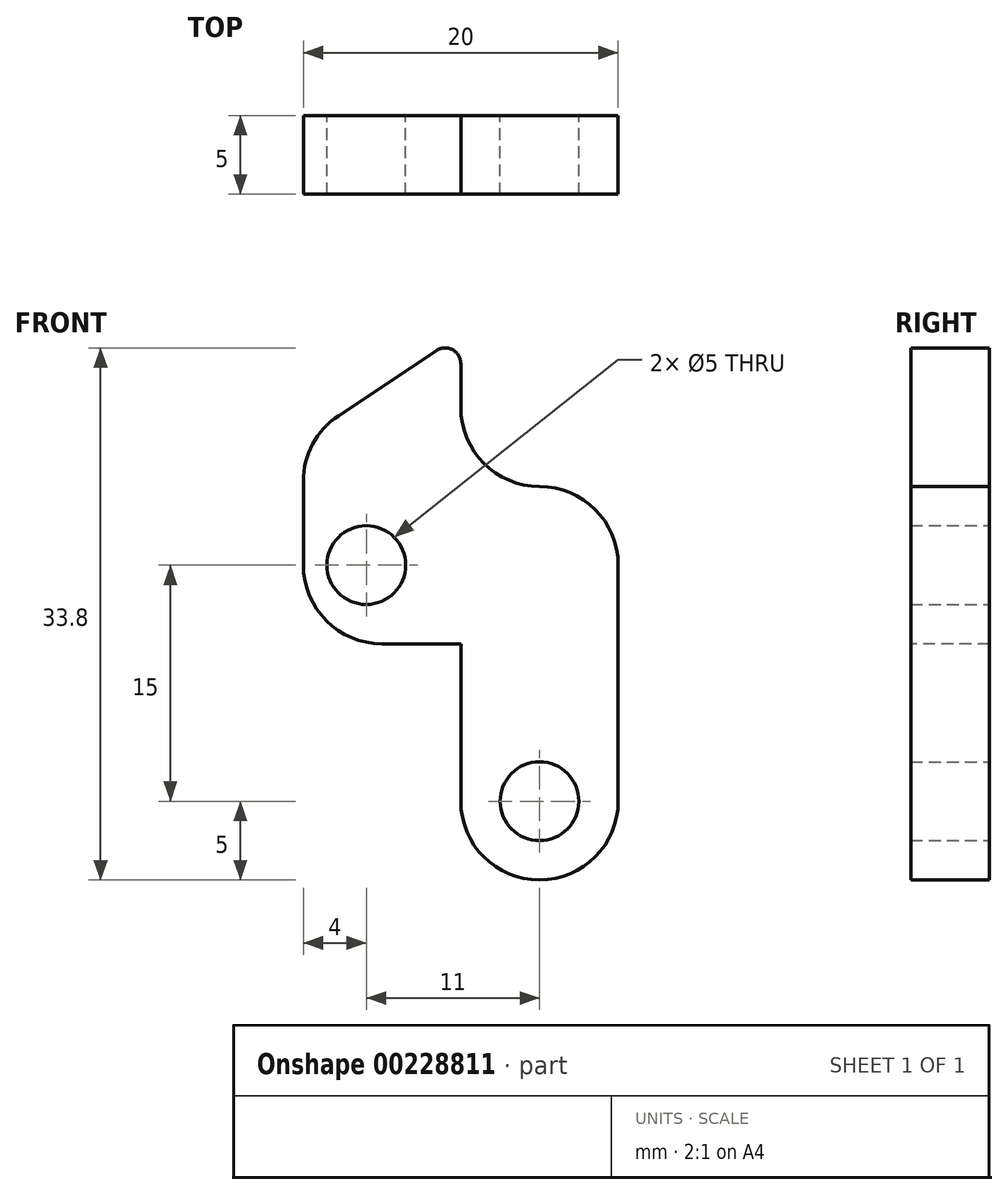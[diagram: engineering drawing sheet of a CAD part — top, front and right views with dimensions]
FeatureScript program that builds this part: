
annotation { "Feature Type Name" : "Feature", "Feature Type Description" : "" }
export const myFeature = defineFeature(function(context is Context, id is Id, definition is map)
    precondition{}
    {
        {
            var Q0;
            Q0=qCreatedBy(makeId("Front.planeOp"),FACE);
            var sketch = newSketch(context, id + "F0", { "sketchPlane" : qUnion([Q0])});
            skLineSegment(sketch, "E0.bottom", {"start": v(-10, 23) * mm, "end": v(0, 23) * mm});
            skLineSegment(sketch, "E0.top", {"start": v(-10, 0) * mm, "end": v(0, 0) * mm});
            skLineSegment(sketch, "E0.left", {"start": v(-10, 23) * mm, "end": v(-10, 0) * mm});
            skLineSegment(sketch, "E0.right", {"start": v(0, 23) * mm, "end": v(0, 0) * mm});
            skLineSegment(sketch, "E1.bottom", {"start": v(10, 0) * mm, "end": v(0, 0) * mm});
            skLineSegment(sketch, "E1.top", {"start": v(10, 10) * mm, "end": v(0, 10) * mm});
            skLineSegment(sketch, "E1.left", {"start": v(10, 0) * mm, "end": v(10, 10) * mm});
            skLineSegment(sketch, "E1.right", {"start": v(0, 0) * mm, "end": v(0, 10) * mm});
            skCircle(sketch, "E2", {"center": v(-6, 5) * mm, "radius": 2.5 * mm});
            skSolve(sketch);
        }
        {
            var Q0;
            Q0=makeQuery(id+"F0.imprint","IMPRINT",FACE,{"disambiguationData":[TD([[makeQuery(id+"F0.imprint","IMPRINT",EDGE,{"derivedFrom":sQuery(id+"F0.wireOp",EDGE,"E0.bottom")}),-1.0]])]});
            var Q1;
            Q1=makeQuery(id+"F0.imprint","IMPRINT",FACE,{"disambiguationData":[TD([[makeQuery(id+"F0.imprint","IMPRINT",EDGE,{"derivedFrom":sQuery(id+"F0.wireOp",EDGE,"E1.bottom")}),-1.0]])]});
            extrude(context, id + "F1", {"entities" : qUnion([Q0, Q1]), "endBound" : BoundingType.SYMMETRIC, "depth" : 5 * mm});
        }
        {
            var Q0;
            Q0=makeQuery(id+"F1.opExtrude","SWEPT_EDGE",EDGE,{"disambiguationData":[OSD([sQuery(id+"F0.wireOp",EDGE,"E0.bottom"),sQuery(id+"F0.wireOp",EDGE,"E0.left")])]});
            chamfer(context, id + "F2", {"entities" : qUnion([Q0]), "chamferType" : ChamferType.TWO_OFFSETS, "width1" : 10 * mm, "oppositeDirection" : false, "width2" : 15 * mm, "tangentPropagation" : true});
        }
        {
            var Q0;
            Q0=makeQuery(id+"F1.opExtrude","SWEPT_EDGE",EDGE,{"disambiguationData":[OSD([sQuery(id+"F0.wireOp",EDGE,"E0.right"),sQuery(id+"F0.wireOp",EDGE,"E1.top"),sQuery(id+"F0.wireOp",EDGE,"E1.right")])]});
            var Q1;
            Q1=makeQuery(id+"F1.opExtrude","SWEPT_EDGE",EDGE,{"disambiguationData":[OSD([sQuery(id+"F0.wireOp",EDGE,"E1.top"),sQuery(id+"F0.wireOp",EDGE,"E1.left")])]});
            var Q2;
            Q2=makeQuery(id+"F1.opExtrude","SWEPT_EDGE",EDGE,{"disambiguationData":[OSD([sQuery(id+"F0.wireOp",EDGE,"E1.bottom"),sQuery(id+"F0.wireOp",EDGE,"E1.left")])]});
            var Q3;
            Q3=makeQuery(id+"F1.opExtrude","SWEPT_EDGE",EDGE,{"disambiguationData":[OSD([sQuery(id+"F0.wireOp",EDGE,"E0.top"),sQuery(id+"F0.wireOp",EDGE,"E0.left")])]});
            fillet(context, id + "F3", {"entities" : qUnion([Q0, Q1, Q2, Q3]), "radius" : 5 * mm, "tangentPropagation" : true, "allowEdgeOverflow" : false});
        }
        {
            var Q0;
            Q0=makeQuery(id+"F2.opChamfer","BLEND_EDGE",EDGE,{"blendedFrom":[makeQuery(id+"F1.opExtrude","SWEPT_EDGE",EDGE,{"disambiguationData":[OSD([sQuery(id+"F0.wireOp",EDGE,"E0.bottom"),sQuery(id+"F0.wireOp",EDGE,"E0.left")])]}),makeQuery(id+"F1.opExtrude","SWEPT_FACE",FACE,{"disambiguationData":[OSD([sQuery(id+"F0.wireOp",EDGE,"E0.right")])]})],"blendedInto":[makeQuery(id+"F1.opExtrude","SWEPT_FACE",FACE,{"disambiguationData":[OSD([sQuery(id+"F0.wireOp",EDGE,"E0.right")])]})]});
            fillet(context, id + "F4", {"entities" : qUnion([Q0]), "radius" : 1 * mm, "tangentPropagation" : true, "allowEdgeOverflow" : false});
        }
        {
            var Q0;
            {var subQ0=sQuery(id+"F0.wireOp",EDGE,"E0.left");Q0=makeQuery(id+"F2.opChamfer","BLEND_EDGE",EDGE,{"blendedFrom":[makeQuery(id+"F1.opExtrude","SWEPT_EDGE",EDGE,{"disambiguationData":[OSD([sQuery(id+"F0.wireOp",EDGE,"E0.bottom"),subQ0])]}),makeQuery(id+"F1.opExtrude","SWEPT_FACE",FACE,{"disambiguationData":[OSD([subQ0])]})],"blendedInto":[makeQuery(id+"F1.opExtrude","SWEPT_FACE",FACE,{"disambiguationData":[OSD([subQ0])]})]});}
            fillet(context, id + "F5", {"entities" : qUnion([Q0]), "radius" : 5 * mm, "tangentPropagation" : true, "allowEdgeOverflow" : false});
        }
        {
            var Q0;
            Q0=makeQuery(id+"F1.opExtrude","CAP_FACE",FACE,{"disambiguationData":[OSD([sQuery(id+"F0.wireOp",EDGE,"E0.bottom"),sQuery(id+"F0.wireOp",EDGE,"E0.top"),sQuery(id+"F0.wireOp",EDGE,"E0.left"),sQuery(id+"F0.wireOp",EDGE,"E0.right"),sQuery(id+"F0.wireOp",EDGE,"E1.bottom"),sQuery(id+"F0.wireOp",EDGE,"E1.top"),sQuery(id+"F0.wireOp",EDGE,"E1.left"),sQuery(id+"F0.wireOp",EDGE,"E2")])],"isStart":false});
            var sketch = newSketch(context, id + "F6", { "sketchPlane" : qUnion([Q0])});
            skLineSegment(sketch, "E3.bottom", {"start": v(0, 5) * mm, "end": v(10, 5) * mm});
            skLineSegment(sketch, "E3.top", {"start": v(0, -15) * mm, "end": v(10, -15) * mm});
            skLineSegment(sketch, "E3.left", {"start": v(10, 5) * mm, "end": v(10, -15) * mm});
            skLineSegment(sketch, "E3.right", {"start": v(0, 5) * mm, "end": v(0, -15) * mm});
            skCircle(sketch, "E4", {"center": v(5, 5) * mm, "radius": 5 * mm});
            skSolve(sketch);
        }
        {
            var Q0;
            {var subQ1=sQuery(id+"F6.wireOp",EDGE,"E3.top");Q0=makeQuery(id+"F6.imprint","IMPRINT",FACE,{"disambiguationData":[TD([[makeQuery(id+"F6.imprint","IMPRINT",EDGE,{"derivedFrom":subQ1}),1.0]])]});}
            var Q1;
            Q1=makeQuery(id+"F1.opExtrude","CAP_FACE",FACE,{"disambiguationData":[OSD([sQuery(id+"F0.wireOp",EDGE,"E0.bottom"),sQuery(id+"F0.wireOp",EDGE,"E0.top"),sQuery(id+"F0.wireOp",EDGE,"E0.left"),sQuery(id+"F0.wireOp",EDGE,"E0.right"),sQuery(id+"F0.wireOp",EDGE,"E1.bottom"),sQuery(id+"F0.wireOp",EDGE,"E1.top"),sQuery(id+"F0.wireOp",EDGE,"E1.left"),sQuery(id+"F0.wireOp",EDGE,"E2")])],"isStart":true});
            extrude(context, id + "F7", {"entities" : qUnion([Q0]), "operationType" : NewBodyOperationType.ADD, "endBound" : BoundingType.UP_TO_SURFACE, "oppositeDirection" : true, "endBoundEntityFace" : qUnion([Q1]), "depth" : 25 * mm});
        }
        {
            var Q0;
            Q0=makeQuery(id+"F7.opExtrude","SWEPT_EDGE",EDGE,{"disambiguationData":[OSD([sQuery(id+"F0.wireOp",EDGE,"E0.top"),sQuery(id+"F0.wireOp",EDGE,"E1.bottom"),sQuery(id+"F6.wireOp",EDGE,"E3.right")])]});
            var Q1;
            Q1=makeQuery(id+"F7.opExtrude","SWEPT_EDGE",EDGE,{"disambiguationData":[OSD([sQuery(id+"F6.wireOp",EDGE,"E3.top"),sQuery(id+"F6.wireOp",EDGE,"E3.right")])]});
            var Q2;
            Q2=makeQuery(id+"F7.opExtrude","SWEPT_EDGE",EDGE,{"disambiguationData":[OSD([sQuery(id+"F6.wireOp",EDGE,"E3.top"),sQuery(id+"F6.wireOp",EDGE,"E3.left")])]});
            fillet(context, id + "F8", {"entities" : qUnion([Q0, Q1, Q2]), "radius" : 5 * mm, "tangentPropagation" : true, "allowEdgeOverflow" : false});
        }
        {
            var Q0;
            {var subQ0=sQuery(id+"F0.wireOp",EDGE,"E2");var subQ1=sQuery(id+"F0.wireOp",EDGE,"E1.left");var subQ2=sQuery(id+"F0.wireOp",EDGE,"E1.top");var subQ3=sQuery(id+"F0.wireOp",EDGE,"E1.bottom");var subQ4=sQuery(id+"F0.wireOp",EDGE,"E0.right");var subQ5=sQuery(id+"F0.wireOp",EDGE,"E0.left");var subQ6=sQuery(id+"F0.wireOp",EDGE,"E0.top");var subQ7=sQuery(id+"F0.wireOp",EDGE,"E0.bottom");Q0=makeQuery(id+"F7.boolean.opBoolean","MERGE",FACE,{"derivedFrom":[makeQuery(id+"F1.opExtrude","CAP_FACE",FACE,{"disambiguationData":[OSD([subQ7,subQ6,subQ5,subQ4,subQ3,subQ2,subQ1,subQ0])],"isStart":true}),makeQuery(id+"F7.opExtrude","CAP_FACE",FACE,{"disambiguationData":[OSD([subQ7,subQ6,subQ5,subQ4,subQ3,subQ2,subQ1,subQ0])],"isStart":false})]});}
            var sketch = newSketch(context, id + "F9", { "sketchPlane" : qUnion([Q0])});
            skCircle(sketch, "E5", {"center": v(-5, -10) * mm, "radius": 2.5 * mm});
            skSolve(sketch);
        }
        {
            var Q0;
            Q0=makeQuery(id+"F9.imprint","IMPRINT",FACE,{"disambiguationData":[TD([[makeQuery(id+"F9.imprint","IMPRINT",EDGE,{"derivedFrom":sQuery(id+"F9.wireOp",EDGE,"E5")}),1.0]])]});
            extrude(context, id + "F10", {"entities" : qUnion([Q0]), "operationType" : NewBodyOperationType.REMOVE, "endBound" : BoundingType.THROUGH_ALL, "oppositeDirection" : true, "depth" : 25 * mm});
        }
    });
